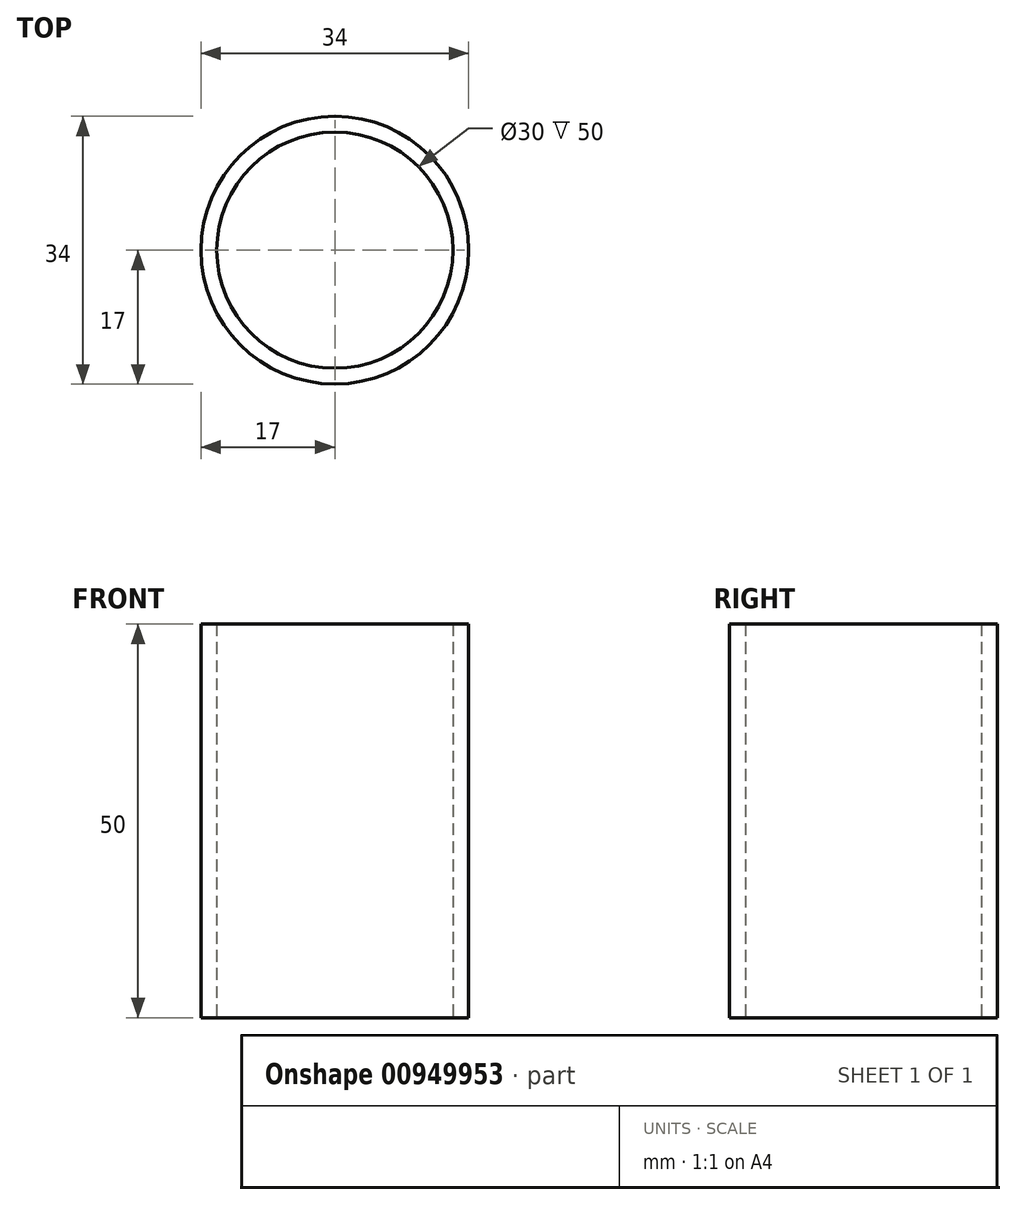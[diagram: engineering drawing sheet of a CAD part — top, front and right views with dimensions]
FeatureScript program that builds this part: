
annotation { "Feature Type Name" : "Feature", "Feature Type Description" : "" }
export const myFeature = defineFeature(function(context is Context, id is Id, definition is map)
    precondition{}
    {
        {
            var Q0;
            Q0=qCreatedBy(makeId("Top.planeOp"),FACE);
            var sketch = newSketch(context, id + "F0", { "sketchPlane" : qUnion([Q0])});
            skCircle(sketch, "E0", {"center": v(0, 0) * mm, "radius": 15 * mm});
            skCircle(sketch, "E1", {"center": v(0, 0) * mm, "radius": 17 * mm});
            skSolve(sketch);
        }
        {
            var Q0;
            Q0=makeQuery(id+"F0.imprint","IMPRINT",FACE,{"disambiguationData":[TD([[makeQuery(id+"F0.imprint","IMPRINT",EDGE,{"derivedFrom":sQuery(id+"F0.wireOp",EDGE,"E0")}),-1.0]])]});
            extrude(context, id + "F1", {"entities" : qUnion([Q0]), "depth" : 50 * mm, "offsetDistance" : 25 * mm});
        }
    });
